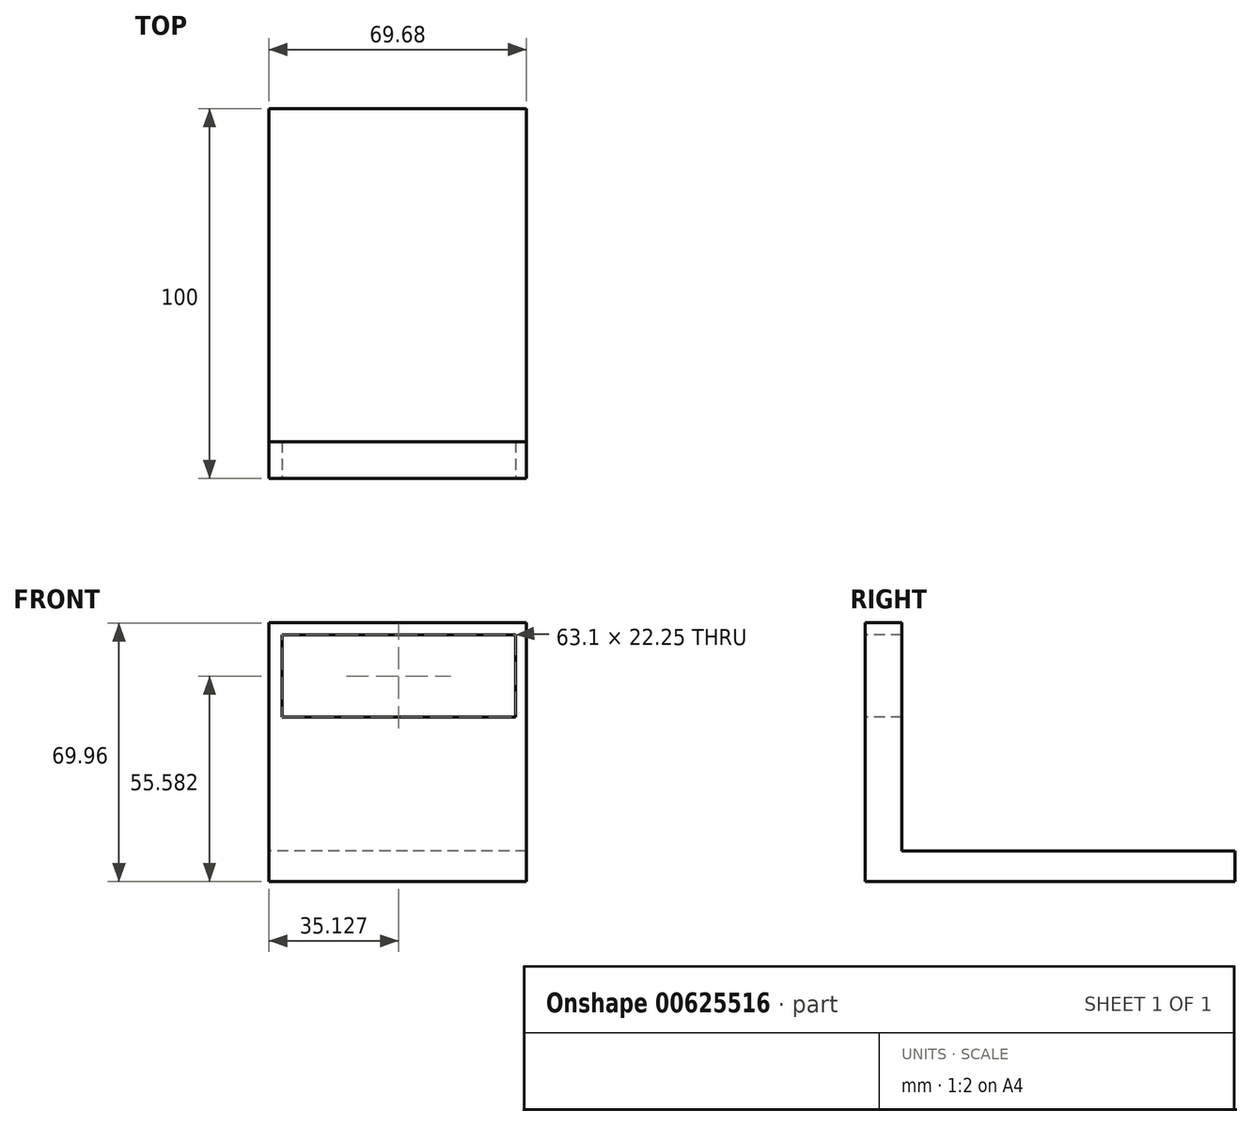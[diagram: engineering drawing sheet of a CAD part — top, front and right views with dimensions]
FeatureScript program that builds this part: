
annotation { "Feature Type Name" : "Feature", "Feature Type Description" : "" }
export const myFeature = defineFeature(function(context is Context, id is Id, definition is map)
    precondition{}
    {
        {
            var Q0;
            Q0=qCreatedBy(makeId("Front.planeOp"),FACE);
            var sketch = newSketch(context, id + "F0", { "sketchPlane" : qUnion([Q0])});
            skLineSegment(sketch, "E0.bottom", {"start": v(-34.84, -34.98) * mm, "end": v(34.84, -34.98) * mm});
            skLineSegment(sketch, "E0.top", {"start": v(-34.84, 34.98) * mm, "end": v(34.84, 34.98) * mm});
            skLineSegment(sketch, "E0.left", {"start": v(-34.84, -34.98) * mm, "end": v(-34.84, 34.98) * mm});
            skLineSegment(sketch, "E0.right", {"start": v(34.84, -34.98) * mm, "end": v(34.84, 34.98) * mm});
            skPoint(sketch, "E0.middle", {"position": v(0, 0) * mm});
            skSolve(sketch);
        }
        {
            var Q0;
            Q0=makeQuery(id+"F0.imprint","IMPRINT",FACE,{"disambiguationData":[TD([[makeQuery(id+"F0.imprint","IMPRINT",EDGE,{"derivedFrom":sQuery(id+"F0.wireOp",EDGE,"E0.bottom")}),1.0]])]});
            extrude(context, id + "F1", {"entities" : qUnion([Q0]), "depth" : 100 * mm, "offsetDistance" : 25 * mm});
        }
        {
            var Q0;
            Q0=makeQuery(id+"F1.opExtrude","CAP_FACE",FACE,{"disambiguationData":[OSD([sQuery(id+"F0.wireOp",EDGE,"E0.bottom"),sQuery(id+"F0.wireOp",EDGE,"E0.top"),sQuery(id+"F0.wireOp",EDGE,"E0.left"),sQuery(id+"F0.wireOp",EDGE,"E0.right")])],"isStart":true});
            var sketch = newSketch(context, id + "F2", { "sketchPlane" : qUnion([Q0])});
            skLineSegment(sketch, "E1.bottom", {"start": v(-34.84, 34.98) * mm, "end": v(34.84, 34.98) * mm});
            skLineSegment(sketch, "E1.top", {"start": v(-34.84, -26.63) * mm, "end": v(34.84, -26.63) * mm});
            skLineSegment(sketch, "E1.left", {"start": v(-34.84, 34.98) * mm, "end": v(-34.84, -26.63) * mm});
            skLineSegment(sketch, "E1.right", {"start": v(34.84, 34.98) * mm, "end": v(34.84, -26.63) * mm});
            skSolve(sketch);
        }
        {
            var Q0;
            Q0 = qSketchRegion(id + "F2", true);
            extrude(context, id + "F3", {"entities" : qUnion([Q0]), "operationType" : NewBodyOperationType.REMOVE, "oppositeDirection" : true, "depth" : 90 * mm, "offsetDistance" : 25 * mm});
        }
        {
            var Q0;
            Q0=makeQuery(id+"F1.opExtrude","CAP_FACE",FACE,{"disambiguationData":[OSD([sQuery(id+"F0.wireOp",EDGE,"E0.bottom"),sQuery(id+"F0.wireOp",EDGE,"E0.top"),sQuery(id+"F0.wireOp",EDGE,"E0.left"),sQuery(id+"F0.wireOp",EDGE,"E0.right")])],"isStart":false});
            var sketch = newSketch(context, id + "F4", { "sketchPlane" : qUnion([Q0])});
            skLineSegment(sketch, "E2.bottom", {"start": v(-31.26, 31.73) * mm, "end": v(31.84, 31.73) * mm});
            skLineSegment(sketch, "E2.top", {"start": v(-31.26, 9.48) * mm, "end": v(31.84, 9.48) * mm});
            skLineSegment(sketch, "E2.left", {"start": v(-31.26, 31.73) * mm, "end": v(-31.26, 9.48) * mm});
            skLineSegment(sketch, "E2.right", {"start": v(31.84, 31.73) * mm, "end": v(31.84, 9.48) * mm});
            skSolve(sketch);
        }
        {
            var Q0;
            Q0 = qSketchRegion(id + "F4", true);
            extrude(context, id + "F5", {"entities" : qUnion([Q0]), "operationType" : NewBodyOperationType.REMOVE, "oppositeDirection" : true, "depth" : 25 * mm, "offsetDistance" : 25 * mm});
        }
    });
